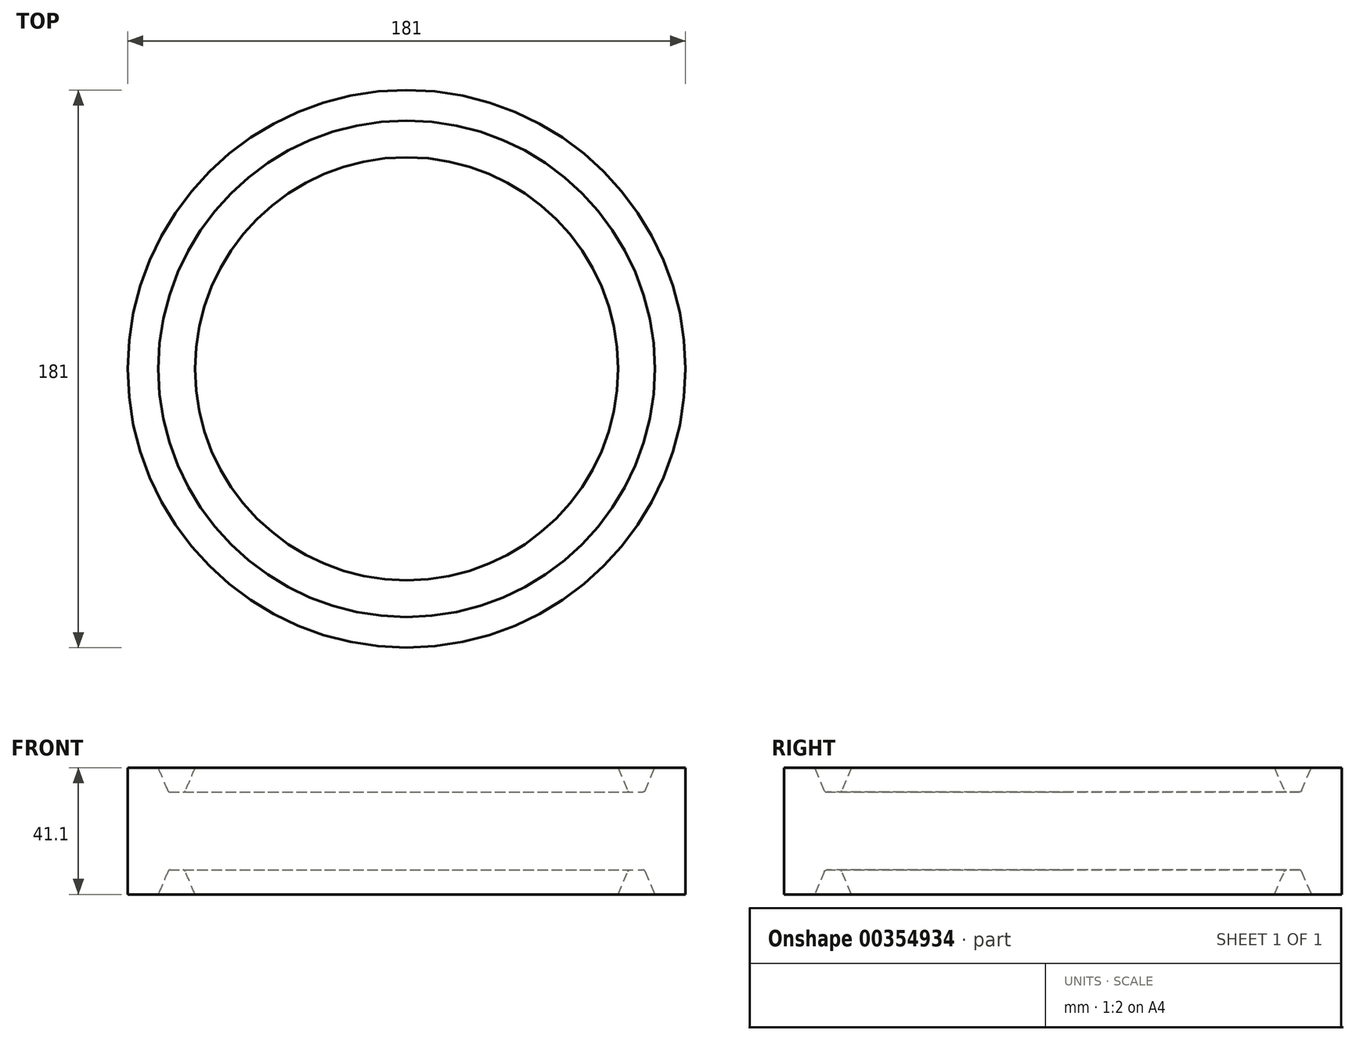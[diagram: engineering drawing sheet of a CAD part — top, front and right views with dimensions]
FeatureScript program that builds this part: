
annotation { "Feature Type Name" : "Feature", "Feature Type Description" : "" }
export const myFeature = defineFeature(function(context is Context, id is Id, definition is map)
    precondition{}
    {
        {
            var Q0;
            Q0=qCreatedBy(makeId("Top.planeOp"),FACE);
            var sketch = newSketch(context, id + "F0", { "sketchPlane" : qUnion([Q0])});
            skCircle(sketch, "E0", {"center": v(-117.5, 0) * mm, "radius": 90.5 * mm});
            skSolve(sketch);
        }
        {
            var Q0;
            Q0=makeQuery(id+"F0.imprint","IMPRINT",FACE,{"disambiguationData":[TD([[makeQuery(id+"F0.imprint","IMPRINT",EDGE,{"derivedFrom":sQuery(id+"F0.wireOp",EDGE,"E0")}),1.0]])]});
            extrude(context, id + "F1", {"entities" : qUnion([Q0]), "depth" : 41.1 * mm});
        }
        {
            var Q0;
            Q0=qCreatedBy(makeId("Front.planeOp"),FACE);
            var sketch = newSketch(context, id + "F2", { "sketchPlane" : qUnion([Q0])});
            skLineSegment(sketch, "E1", {"start": v(-186.16, 41.1) * mm, "end": v(-189.31, 33.67) * mm});
            skLineSegment(sketch, "E2", {"start": v(-194.18, 33.18) * mm, "end": v(-190.05, 33.18) * mm});
            skLineSegment(sketch, "E3", {"start": v(-194.92, 33.67) * mm, "end": v(-198.07, 41.1) * mm});
            skLineSegment(sketch, "E4", {"start": v(-192.12, 33.18) * mm, "end": v(-192.12, 41.1) * mm, "construction": true});
            skLineSegment(sketch, "E5", {"start": v(-117.5, 41.1) * mm, "end": v(-117.5, 0) * mm, "construction": true});
            skPoint(sketch, "E6.visualSharp", {"position": v(-194.7, 33.18) * mm});
            skArc(sketch, "E6.filletArc", {"start": v(-194.92, 33.67) * mm, "mid": v(-194.62, 33.31) * mm, "end": v(-194.18, 33.18) * mm});
            skPoint(sketch, "E7.visualSharp", {"position": v(-189.52, 33.18) * mm});
            skArc(sketch, "E7.filletArc", {"start": v(-190.05, 33.18) * mm, "mid": v(-189.6, 33.31) * mm, "end": v(-189.31, 33.67) * mm});
            skLineSegment(sketch, "E8", {"start": v(-198.07, 41.1) * mm, "end": v(-186.16, 41.1) * mm});
            skPoint(sketch, "E9", {"position": v(-117.5, 20.55) * mm});
            skLineSegment(sketch, "E10", {"start": v(-396.45, 20.55) * mm, "end": v(161.45, 20.55) * mm, "construction": true});
            skArc(sketch, "E11.MirrorCS", {"start": v(-194.18, 33.18) * mm, "mid": v(-194.62, 33.31) * mm, "end": v(-194.92, 33.67) * mm});
            skArc(sketch, "E12.MirrorCS", {"start": v(-189.31, 33.67) * mm, "mid": v(-189.6, 33.31) * mm, "end": v(-190.05, 33.18) * mm});
            skLineSegment(sketch, "E13.MirrorCS", {"start": v(-190.05, 33.18) * mm, "end": v(-194.18, 33.18) * mm});
            skLineSegment(sketch, "E14.MirrorCS", {"start": v(-189.31, 33.67) * mm, "end": v(-186.16, 41.1) * mm});
            skLineSegment(sketch, "E15.MirrorCS", {"start": v(-198.07, 41.1) * mm, "end": v(-194.92, 33.67) * mm});
            skLineSegment(sketch, "E16.MirrorCS", {"start": v(-186.16, 41.1) * mm, "end": v(-198.07, 41.1) * mm});
            skArc(sketch, "E17.MirrorCS", {"start": v(-190.05, 7.92) * mm, "mid": v(-189.6, 7.79) * mm, "end": v(-189.31, 7.43) * mm});
            skArc(sketch, "E18.MirrorCS", {"start": v(-194.92, 7.43) * mm, "mid": v(-194.62, 7.79) * mm, "end": v(-194.18, 7.92) * mm});
            skArc(sketch, "E19.MirrorCS", {"start": v(-194.18, 7.92) * mm, "mid": v(-194.62, 7.79) * mm, "end": v(-194.92, 7.43) * mm});
            skArc(sketch, "E20.MirrorCS", {"start": v(-189.31, 7.43) * mm, "mid": v(-189.6, 7.79) * mm, "end": v(-190.05, 7.92) * mm});
            skLineSegment(sketch, "E21.MirrorCS", {"start": v(-190.05, 7.92) * mm, "end": v(-194.18, 7.92) * mm});
            skPoint(sketch, "E22.MirrorP", {"position": v(-189.52, 7.92) * mm});
            skPoint(sketch, "E23.MirrorP", {"position": v(-194.7, 7.92) * mm});
            skLineSegment(sketch, "E24.MirrorCS", {"start": v(-194.18, 7.92) * mm, "end": v(-190.05, 7.92) * mm});
            skLineSegment(sketch, "E25.MirrorCS", {"start": v(-198.07, 0) * mm, "end": v(-186.16, 0) * mm});
            skLineSegment(sketch, "E26.MirrorCS", {"start": v(-198.07, 0) * mm, "end": v(-194.92, 7.43) * mm});
            skLineSegment(sketch, "E27.MirrorCS", {"start": v(-189.31, 7.43) * mm, "end": v(-186.16, 0) * mm});
            skLineSegment(sketch, "E28.MirrorCS", {"start": v(-192.12, 7.92) * mm, "end": v(-192.12, 0) * mm, "construction": true});
            skLineSegment(sketch, "E29.MirrorCS", {"start": v(-194.92, 7.43) * mm, "end": v(-198.07, 0) * mm});
            skLineSegment(sketch, "E30.MirrorCS", {"start": v(-186.16, 0) * mm, "end": v(-189.31, 7.43) * mm});
            skLineSegment(sketch, "E31.MirrorCS", {"start": v(-186.16, 0) * mm, "end": v(-198.07, 0) * mm});
            skSolve(sketch);
        }
        {
            var Q0;
            Q0 = qSketchRegion(id + "F2", true);
            var Q1;
            Q1=sQuery(id+"F2.wireOp",EDGE,"E5");
            revolve(context, id + "F3", {"operationType" : NewBodyOperationType.REMOVE, "entities" : qUnion([Q0]), "axis" : qUnion([Q1]), "revolveType" : RevolveType.FULL, "oppositeDirection" : true});
        }
    });
